# Revit family: Legrand_Lighting_Management_DALI_Presence_Sensor_Ceiling
name_source: partatom
category: Dispositifs d'éclairage
units: mm (PartAtom-declared; Revit-internal decimal feet)

## family parameters
Conserver l'orientation des annotations = Non
Cote de connecteur circulaire = Utiliser le diamètre
Couper avec des vides une fois chargée = Non
Hôte = Face
Partagée = Non
Point de calcul de pièce = Non
Type d'élément = Normal

## types (2) — shared parameters
Alarm function = Non
Collecteur de terre = Non
Colour = White
Constant light control = Oui
Cosses d'artère secondaire = Non
Detection angle horizontal (MAX) (°) = 360
Detection angle horizontal (MIN) (°) = 360
Dim function with dimmer basic element = Oui
Elévation par défaut = 1219 mm
Fabricant = Legrand
Forced switch off = Oui
Frequency (MAX) (Hz) = 60
Frequency (MIN) (Hz) = 50
General Conditions of Use = https://export.legrand.com
HVAC-control = Non
Liaison neutre = Non
Max. duty cycle (mn) = 30
Maximum mounting height (m) = 2.5
Min. switch-on time (s) = 5
Model = Presence detector
Mounting method = Flush mounted (plaster)
Nominal voltage (V) = 16
RAL-number (akin) = 9006
Remote operation = Oui
Response value luminosity adjustable = Oui
Response value sensitivity adjustable = Oui
Substation input = Non
Suitable for wireless transmission = Oui
Temperature (MAX) (°C) = 45
Temperature (MIN) (°C) = -5
URL = http://www.legrandoc.com
zero-valued in all types: Max. starting current (A), Max. switching power (W), Response value luminosity (MAX) (lx), Response value luminosity (MIN) (lx)

## per-type parameters (varying)
| type | COULOIR | DUAL-TECH | Degree of protection (IP) | Description | Diameter detection range on floor (m) | Max. transmission range frontally (m) | Max. transmission range sideways (m) | Modèle |
| Corridor | Oui | Non | IP41 | DALI lighting management sensor - 360° IR dual detection - side range 2 x 12 m | 12 | 12 | 12 | 048936 |
| DUAL-TECH | Non | Oui | IP20 | DALI lighting management sensor - 360° IR and ultrasonic - range Ø 8 m | 8 | 8 | 8 | 048935 |
